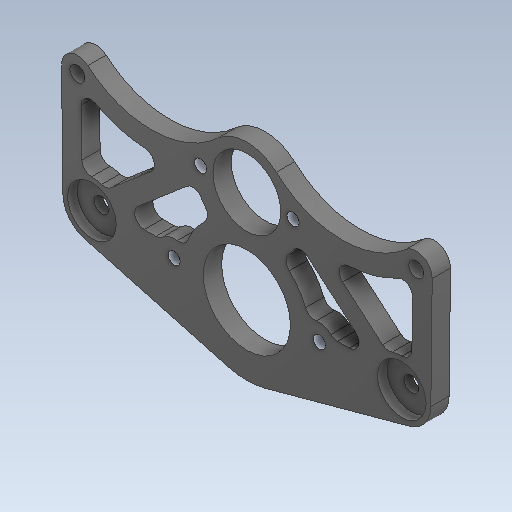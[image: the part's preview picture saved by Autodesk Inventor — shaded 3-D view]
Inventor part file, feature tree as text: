
AUTODESK INVENTOR PART (.ipt)
format: ipt  version: 2020 (Build 240168000, 168)  size: 207,360 bytes
history: native  units: in
note: dims shown in document units (in); Inventor stores cm internally (conversion verified against a paired STEP export)
features: fillet x1
ambient origin geometry x8: Origin, YZ Plane, XZ Plane, XY Plane, X Axis, Y Axis, Z Axis, Center Point
bodies: Solid1 (feature_tree)
feature tree (1):
  fillet  "Fillet2"  [1 undecoded]
note: 1 required parameter value undecoded (feature->parameter linkage not recoverable at this tier; creation-order binding heuristic only, values carry confidence <= 0.55)
